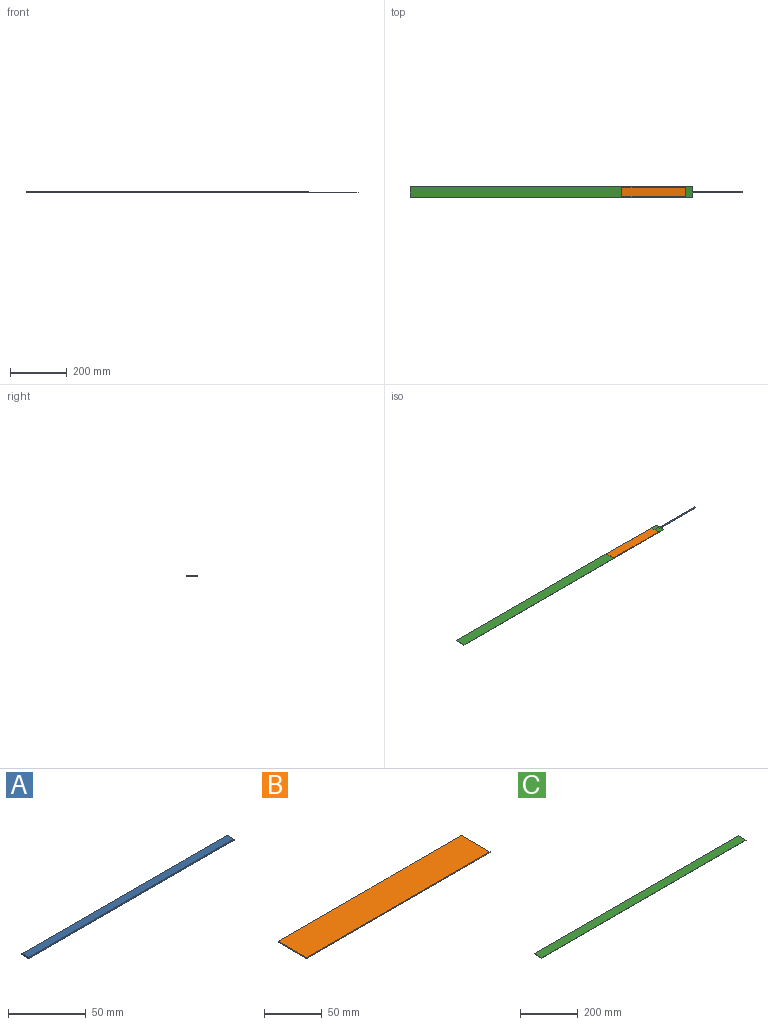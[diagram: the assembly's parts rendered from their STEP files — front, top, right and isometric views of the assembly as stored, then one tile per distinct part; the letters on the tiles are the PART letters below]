
ASSEMBLY  parts=3 mates=2
PART A: 6 faces, bbox 187x6.3x1 mm
  f0: plane 187x1mm, normal (0,1,0), area 187mm2, adj f1,f3,f4,f5
  f1: plane 6.3x1mm, normal (-1,0,0), area 6.3mm2, adj f0,f2,f4,f5
  f2: plane 187x1mm, normal (0,-1,0), area 187mm2, adj f1,f3,f4,f5
  f3: plane 6.3x1mm, normal (1,0,0), area 6.3mm2, adj f0,f2,f4,f5
  f4: plane 187x6.3mm, normal (0,0,1), area 1178.1mm2, adj f0,f1,f2,f3
  f5: plane 187x6.3mm, normal (0,0,-1), area 1178.1mm2, adj f0,f1,f2,f3
PART B: 6 faces, bbox 225x35x1 mm
  f0: plane 225x1mm, normal (0,1,0), area 225mm2, adj f1,f3,f4,f5
  f1: plane 35x1mm, normal (-1,0,0), area 35mm2, adj f0,f2,f4,f5
  f2: plane 225x1mm, normal (0,-1,0), area 225mm2, adj f1,f3,f4,f5
  f3: plane 35x1mm, normal (1,0,0), area 35mm2, adj f0,f2,f4,f5
  f4: plane 225x35mm, normal (0,0,1), area 7875mm2, adj f0,f1,f2,f3
  f5: plane 225x35mm, normal (0,0,-1), area 7875mm2, adj f0,f1,f2,f3
PART C: 6 faces, bbox 1000x38x1 mm
  f0: plane 1000x1mm, normal (0,1,0), area 1000mm2, adj f1,f3,f4,f5
  f1: plane 38x1mm, normal (-1,0,0), area 38mm2, adj f0,f2,f4,f5
  f2: plane 1000x1mm, normal (0,-1,0), area 1000mm2, adj f1,f3,f4,f5
  f3: plane 38x1mm, normal (1,0,0), area 38mm2, adj f0,f2,f4,f5
  f4: plane 1000x38mm, normal (0,0,1), area 38000mm2, adj f0,f1,f2,f3
  f5: plane 1000x38mm, normal (0,0,-1), area 38000mm2, adj f0,f1,f2,f3
PLACE A t=(564.96,-3.47,-107.63)mm
PLACE B t=(346.46,-3.47,-105.63)mm
PLACE C t=(-16.54,-3.47,-106.63)mm
MATE fastened C.f5 <-> A.f4  axis (0,0,-1) through (483.46,-3.47,-106.63)mm
MATE fastened B.f5 <-> C.f4  axis (0,0,-1) through (458.46,-3.47,-105.63)mm
